# Revit family: EKF_EE_БоковыеПанелиЦоколяTrivia_AVERES
name_source: partatom
category: Электрооборудование
units: mm (PartAtom-declared; Revit-internal decimal feet)

## family parameters
Всегда вертикально = Нет
На основе рабочей плоскости = Да
Общий = Да
При загрузке вырезать с полостями = Нет
Размер круглого соединителя = Использовать диаметр
Тип детали = Силовой щит
Точка расчета площади = Нет

## types (3) — shared parameters
ADSK_Единица измерения = шт.
ADSK_Завод-изготовитель = EKF
ADSK_Количество = 1
ADSK_Марка = Боковые панели цоколя
ADSK_Материал = RAL 7035_Сталь
ADSK_Обозначение = Боковые панели цоколя
ADSK_Размер_Высота = 100 мм
ADSK_Размер_Глубина = 65 мм
Изготовитель = EKF
Отметка по умолчанию = 1219.2 мм
Серия номенклатуры = Averes
Степень защиты IP = -
ТВ = EKF_2_TRIVIA_AVERES
Тип установки = -
zero-valued in all types: ADSK_Масса

## per-type parameters (varying)
| type | ADSK_Код изделия | ADSK_Размер_Ширина | Тип |
| Боковые панели цоколя Г400 EKF AVERES | BSP400 | 259 мм | 483 мм |
| Боковые панели цоколя Г600 EKF AVERES | BSP600 | 459 мм | 484 мм |
| Боковые панели цоколя Г800 EKF AVERES | BSP800 | 659 мм | 485 мм |

note: column(s) folded — value = type name in every type: ADSK_Наименование
